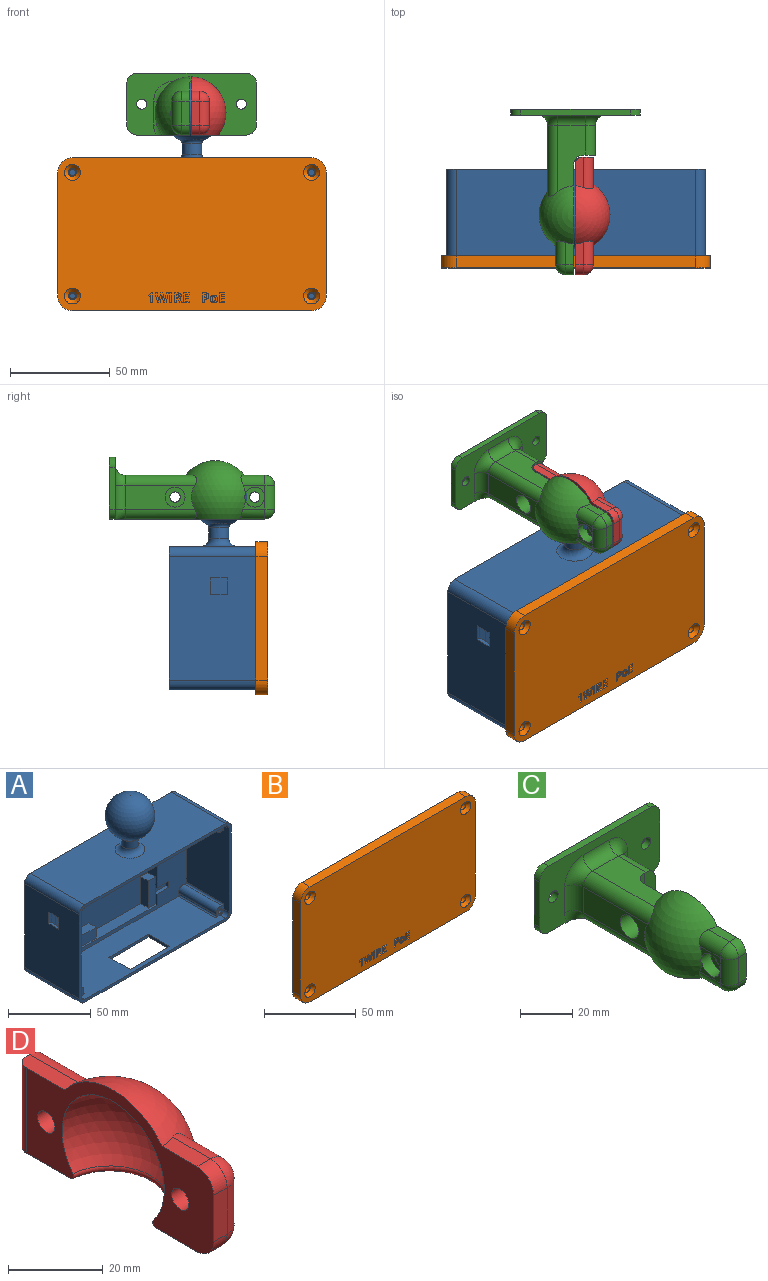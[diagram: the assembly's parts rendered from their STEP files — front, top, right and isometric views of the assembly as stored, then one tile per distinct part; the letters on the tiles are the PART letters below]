
ASSEMBLY  parts=4 mates=1
PART A: 92 faces, bbox 130x46.5x112 mm
  f0: plane 126x68mm, normal (0,-1,0), area 3388mm2, adj f1,f3,f4,f5,f6,f9,f10,f24
  f1: plane 43.9x8mm, normal (-1,0,0), area 302.4mm2, adj f0,f8,f9,f34,f36,f89
  f2: plane 11x9mm, normal (0,-1,0), area 99mm2, adj f6,f9,f81,f82
  f3: plane 120x36.5mm, normal (0,0,1), area 3510mm2, adj f0,f11,f20,f23,f49,f50,f51,f52
  f4: plane 62x36.5mm, normal (-1,0,0), area 2005mm2, adj f0,f11,f20,f21,f59,f66,f70,f74
  f5: plane 62x36.5mm, normal (1,0,0), area 1932.8mm2, adj f0,f11,f22,f23,f45,f46,f47,f48
  f6: plane 120x36.5mm, normal (0,0,-1), area 3994mm2, adj f0,f2,f11,f21,f22,f53,f59,f73
  f7: plane 62x46.5mm, normal (-1,0,0), area 2810.8mm2, adj f11,f15,f18,f19,f45,f46,f47,f48
  f8: plane 86.4x56.4mm, normal (0,-1,0), area 4466.6mm2, adj f1,f9,f24,f25,f26,f27,f28,f29
  f9: plane 85.4x8mm, normal (0,0,-1), area 514.2mm2, adj f0,f1,f2,f8,f24,f37,f38,f44
  f10: plane 8x1.5mm, normal (-1,0,0), area 12mm2, adj f0,f25,f36,f88
  f11: plane 130x72mm, normal (0,-1,0), area 778.3mm2, adj f3,f4,f5,f6,f7,f12,f13,f14
  f12: plane 120x46.5mm, normal (0,0,-1), area 4968mm2, adj f11,f15,f16,f19,f49,f50,f51,f52
  f13: plane 62x46.5mm, normal (1,0,0), area 2883mm2, adj f11,f15,f16,f17
  f14: plane 120x46.5mm, normal (0,0,1), area 5325.5mm2, adj f11,f15,f17,f18,f79
  f15: plane 130x72mm, normal (0,1,0), area 9338.5mm2, adj f7,f12,f13,f14,f16,f17,f18,f19
  f16: cylinder r=5mm len=46.5mm, axis (0,-1,0), area 365.2mm2, adj f11,f12,f13,f15
  f17: cylinder r=5mm len=46.5mm, axis (0,1,0), area 365.2mm2, adj f11,f13,f14,f15
  f18: cylinder r=5mm len=46.5mm, axis (0,-1,0), area 365.2mm2, adj f7,f11,f14,f15
  f19: cylinder r=5mm len=46.5mm, axis (0,1,0), area 365.2mm2, adj f7,f11,f12,f15
  f20: cylinder r=3mm len=4.5mm, axis (0,-1,0), area 21.2mm2, adj f3,f4,f11,f66
  f21: cylinder r=3mm len=4.5mm, axis (0,1,0), area 21.2mm2, adj f4,f6,f11,f59
  f22: cylinder r=3mm len=4.5mm, axis (0,-1,0), area 21.2mm2, adj f5,f6,f11,f53
  f23: cylinder r=3mm len=4.5mm, axis (0,1,0), area 21.2mm2, adj f3,f5,f11,f62
  f24: plane 11.5x8mm, normal (1,0,0), area 92mm2, adj f0,f8,f9,f29
  f25: plane 85.4x8mm, normal (0,0,1), area 546.7mm2, adj f0,f8,f10,f26,f30,f31,f33,f35
  f26: plane 14.9x8mm, normal (1,0,0), area 119.2mm2, adj f0,f8,f25,f27
  f27: plane 8x1mm, normal (0,0,1), area 8mm2, adj f0,f8,f26,f28
  f28: plane 30x8mm, normal (1,0,0), area 240mm2, adj f0,f8,f27,f29
  f29: plane 8x1mm, normal (0,0,-1), area 8mm2, adj f0,f8,f24,f28
  f30: plane 8x6.5mm, normal (-1,0,0), area 52mm2, adj f8,f25,f32,f33
  f31: plane 8x6.5mm, normal (1,0,0), area 52mm2, adj f8,f25,f32,f33
  f32: plane 15x6.5mm, normal (0,0,1), area 97.5mm2, adj f8,f30,f31,f33
  f33: plane 15x8mm, normal (0,-1,0), area 120mm2, adj f25,f30,f31,f32
  f34: plane 6.5x6mm, normal (0,0,1), area 39mm2, adj f1,f8,f35,f36
  f35: plane 20x6.5mm, normal (-1,0,0), area 130mm2, adj f8,f25,f34,f36
  f36: plane 20x6mm, normal (0,-1,0), area 120mm2, adj f1,f10,f25,f34,f35,f86
  f37: plane 6.5x6mm, normal (1,0,0), area 39mm2, adj f8,f9,f43,f44
  f38: plane 6.5x6mm, normal (-1,0,0), area 39mm2, adj f8,f9,f39,f44
  f39: plane 6.5x5mm, normal (0,0,-1), area 32.5mm2, adj f8,f38,f40,f44
  f40: plane 6.5x2mm, normal (1,0,0), area 13mm2, adj f8,f39,f41,f44
  f41: plane 8x6.5mm, normal (0,0,-1), area 52mm2, adj f8,f40,f42,f44
  f42: plane 6.5x2mm, normal (-1,0,0), area 13mm2, adj f8,f41,f43,f44
  f43: plane 13x6.5mm, normal (0,0,-1), area 84.5mm2, adj f8,f37,f42,f44
  f44: plane 26x6mm, normal (0,-1,0), area 140mm2, adj f9,f37,f38,f39,f40,f41,f42,f43
  f45: plane 8.5x2mm, normal (0,0,1), area 17mm2, adj f5,f7,f46,f48
  f46: plane 8.5x2mm, normal (0,1,0), area 17mm2, adj f5,f7,f45,f47
  f47: plane 8.5x2mm, normal (0,0,-1), area 17mm2, adj f5,f7,f46,f48
  f48: plane 8.5x2mm, normal (0,-1,0), area 17mm2, adj f5,f7,f45,f47
  f49: plane 18x2mm, normal (1,0,0), area 36mm2, adj f3,f12,f50,f51
  f50: plane 34x2mm, normal (0,1,0), area 68mm2, adj f3,f12,f49,f52
  f51: plane 34x2mm, normal (0,-1,0), area 68mm2, adj f3,f12,f49,f52
  f52: plane 18x2mm, normal (-1,0,0), area 36mm2, adj f3,f12,f50,f51
  f53: plane 7.03x7.03mm, normal (0,-1,0), area 29.4mm2, adj f5,f6,f22,f54,f55,f75,f76
  f54: cylinder r=3.5mm len=32mm, axis (0,1,0), area 279.1mm2, adj f0,f53,f75,f76
  f55: cylinder r=1.5mm len=32mm, axis (0,1,0), area 301.6mm2, adj f53,f56
  f56: plane 3x3mm, normal (0,-1,0), area 7.1mm2, adj f55
  f57: cylinder r=3.5mm len=32mm, axis (0,1,0), area 279.1mm2, adj f0,f59,f73,f74
  f58: cylinder r=1.5mm len=32mm, axis (0,1,0), area 301.6mm2, adj f59,f60
  f59: plane 7.03x7.03mm, normal (0,-1,0), area 29.4mm2, adj f4,f6,f21,f57,f58,f73,f74
  f60: plane 3x3mm, normal (0,-1,0), area 7.1mm2, adj f58
  f61: cylinder r=3.5mm len=32mm, axis (0,1,0), area 279.1mm2, adj f0,f62,f71,f72
  f62: plane 7.03x7.03mm, normal (0,-1,0), area 29.4mm2, adj f3,f5,f23,f61,f63,f71,f72
  f63: cylinder r=1.5mm len=32mm, axis (0,1,0), area 301.6mm2, adj f62,f64
  f64: plane 3x3mm, normal (0,-1,0), area 7.1mm2, adj f63
  f65: cylinder r=3.5mm len=32mm, axis (0,1,0), area 279.1mm2, adj f0,f66,f69,f70
  f66: plane 7.03x7.03mm, normal (0,-1,0), area 29.4mm2, adj f3,f4,f20,f65,f67,f69,f70
  f67: cylinder r=1.5mm len=32mm, axis (0,1,0), area 301.6mm2, adj f66,f68
  f68: plane 3x3mm, normal (0,-1,0), area 7.1mm2, adj f67
  f69: cylinder r=1mm len=32mm, axis (0,1,0), area 65mm2, adj f0,f3,f65,f66
  f70: cylinder r=1mm len=32mm, axis (0,1,0), area 65mm2, adj f0,f4,f65,f66
  f71: cylinder r=1mm len=32mm, axis (0,1,0), area 65mm2, adj f0,f5,f61,f62
  f72: cylinder r=1mm len=32mm, axis (0,1,0), area 65mm2, adj f0,f3,f61,f62
  f73: cylinder r=1mm len=32mm, axis (0,1,0), area 65mm2, adj f0,f6,f57,f59
  f74: cylinder r=1mm len=32mm, axis (0,1,0), area 65mm2, adj f0,f4,f57,f59
  f75: cylinder r=1mm len=32mm, axis (0,1,0), area 65mm2, adj f0,f5,f53,f54
  f76: cylinder r=1mm len=32mm, axis (0,1,0), area 65mm2, adj f0,f6,f53,f54
  f77: cylinder r=5mm len=10mm, axis (0,0,-1), area 173mm2, adj f79,f91
  f78: sphere r=15mm, area 2702mm2, adj f91
  f79: torus R=9mm, axis (0,0,-1), area 254.8mm2, adj f14,f77
  f80: plane 32x9mm, normal (-1,0,0), area 144mm2, adj f0,f6,f85
  f81: plane 32x9mm, normal (1,0,0), area 144mm2, adj f2,f6,f85
  f82: plane 32x9mm, normal (-1,0,0), area 144mm2, adj f2,f6,f84
  f83: plane 32x9mm, normal (1,0,0), area 144mm2, adj f0,f6,f84
  f84: plane 32x9mm, normal (0,-0.27,-0.96), area 66.5mm2, adj f6,f9,f82,f83
  f85: plane 32x9mm, normal (0,-0.27,-0.96), area 66.5mm2, adj f6,f9,f80,f81
  f86: plane 4.5x1mm, normal (1,0,0), area 4.5mm2, adj f36,f87,f88,f89
  f87: plane 10x4.5mm, normal (0,-1,0), area 45mm2, adj f86,f88,f89,f90
  f88: plane 10x2.5mm, normal (0,0,1), area 25mm2, adj f0,f10,f86,f87,f90
  f89: plane 10x2.5mm, normal (0,0,-1), area 25mm2, adj f0,f1,f86,f87,f90
  f90: plane 4.5x2.5mm, normal (-1,0,0), area 11.3mm2, adj f0,f87,f88,f89
  f91: torus R=7mm, axis (0,0,1), area 77.9mm2, adj f77,f78
PART B: 174 faces, bbox 134.8x6x76.8 mm
  f0: plane 47x3mm, normal (-1,0,0), area 141mm2, adj f1,f166,f170,f171
  f1: plane 125.2x67.2mm, normal (0,1,0), area 3011.4mm2, adj f0,f21,f22,f23,f24,f25,f26,f27
  f2: plane 120x6mm, normal (0,0,-1), area 644mm2, adj f4,f8,f9,f12,f163,f164,f165
  f3: plane 120x3mm, normal (0,0,1), area 284mm2, adj f8,f15,f16,f20,f163,f164,f165
  f4: plane 134.8x76.8mm, normal (0,-1,0), area 10019.4mm2, adj f2,f5,f6,f7,f9,f10,f11,f12
  f5: plane 62x6mm, normal (1,0,0), area 372mm2, adj f4,f8,f9,f10
  f6: plane 120x6mm, normal (0,0,1), area 720mm2, adj f4,f8,f10,f11
  f7: plane 62x6mm, normal (-1,0,0), area 372mm2, adj f4,f8,f11,f12
  f8: plane 134.8x76.8mm, normal (0,1,0), area 732.4mm2, adj f2,f3,f5,f6,f7,f9,f10,f11
  f9: cylinder r=7.4mm len=7.4mm, axis (0,-1,0), area 69.7mm2, adj f2,f4,f5,f8
  f10: cylinder r=7.4mm len=7.4mm, axis (0,1,0), area 69.7mm2, adj f4,f5,f6,f8
  f11: cylinder r=7.4mm len=7.4mm, axis (0,-1,0), area 69.7mm2, adj f4,f6,f7,f8
  f12: cylinder r=7.4mm len=7.4mm, axis (0,1,0), area 69.7mm2, adj f2,f4,f7,f8
  f13: cylinder r=5.4mm len=5.4mm, axis (0,1,0), area 25.4mm2, adj f8,f14,f19,f20
  f14: plane 62x3mm, normal (1,0,0), area 186mm2, adj f8,f13,f15,f20
  f15: cylinder r=5.4mm len=5.4mm, axis (0,1,0), area 25.4mm2, adj f3,f8,f14,f20
  f16: cylinder r=5.4mm len=5.4mm, axis (0,1,0), area 25.4mm2, adj f3,f8,f17,f20
  f17: plane 62x3mm, normal (-1,0,0), area 186mm2, adj f8,f16,f18,f20
  f18: cylinder r=5.4mm len=5.4mm, axis (0,1,0), area 25.4mm2, adj f8,f17,f19,f20
  f19: plane 120x3mm, normal (0,0,-1), area 360mm2, adj f8,f13,f18,f20
  f20: plane 130.8x72.8mm, normal (0,1,0), area 1089.6mm2, adj f3,f13,f14,f15,f16,f17,f18,f19
  f21: plane 62x3mm, normal (-1,0,0), area 186mm2, adj f1,f20,f22,f26
  f22: cylinder r=2.6mm len=3mm, axis (0,1,0), area 12.3mm2, adj f1,f20,f21,f23
  f23: plane 120x3mm, normal (0,0,-1), area 360mm2, adj f1,f20,f22,f24
  f24: cylinder r=2.6mm len=3mm, axis (0,1,0), area 12.3mm2, adj f1,f20,f23,f25
  f25: plane 62x3mm, normal (1,0,0), area 186mm2, adj f1,f20,f24,f27
  f26: cylinder r=2.6mm len=3mm, axis (0,1,0), area 12.3mm2, adj f1,f20,f21,f28
  f27: cylinder r=2.6mm len=3mm, axis (0,1,0), area 12.3mm2, adj f1,f20,f25,f28
  f28: plane 120x3mm, normal (0,0,1), area 360mm2, adj f1,f20,f26,f27
  f29: cylinder r=2mm len=4mm, axis (0,1,0), area 50.3mm2, adj f1,f35
  f30: cylinder r=2mm len=4mm, axis (0,1,0), area 50.3mm2, adj f1,f36
  f31: cylinder r=2mm len=4mm, axis (0,1,0), area 50.3mm2, adj f1,f33
  f32: cylinder r=2mm len=4mm, axis (0,1,0), area 50.3mm2, adj f1,f34
  f33: cone r=2mm half-angle=45deg, axis (0,-1,0), area 53.3mm2, adj f4,f31
  f34: cone r=2mm half-angle=45deg, axis (0,-1,0), area 53.3mm2, adj f4,f32
  f35: cone r=2mm half-angle=45deg, axis (0,-1,0), area 53.3mm2, adj f4,f29
  f36: cone r=2mm half-angle=45deg, axis (0,-1,0), area 53.3mm2, adj f4,f30
  f37: plane 1.2x1mm, normal (0,0,1), area 1.2mm2, adj f4,f38,f60,f61
  f38: plane 4.96x1.26mm, normal (-0.97,0,0.25), area 5.1mm2, adj f4,f37,f39,f61
  f39: plane 1.04x1mm, normal (0,0,-1), area 1mm2, adj f4,f38,f40,f61
  f40: plane 2.71x1mm, normal (0.97,0,-0.23), area 2.8mm2, adj f4,f39,f41,f61
  f41: extruded ~1x0.64mm, area 0.7mm2, adj f4,f40,f42,f61
  f42: extruded ~1x0.66mm, area 0.7mm2, adj f4,f41,f43,f61
  f43: extruded ~1x0.66mm, area 0.7mm2, adj f4,f42,f44,f61
  f44: extruded ~1x0.57mm, area 0.6mm2, adj f4,f43,f45,f61
  f45: plane 2.78x1mm, normal (-0.97,0,-0.25), area 2.9mm2, adj f4,f44,f46,f61
  f46: plane 1x0.99mm, normal (0,0,-1), area 1mm2, adj f4,f45,f47,f61
  f47: plane 2.78x1mm, normal (0.97,0,-0.25), area 2.9mm2, adj f4,f46,f48,f61
  f48: extruded ~1x0.63mm, area 0.6mm2, adj f4,f47,f49,f61
  f49: extruded ~1x0.6mm, area 0.6mm2, adj f4,f48,f50,f61
  f50: extruded ~1.3x1mm, area 1.3mm2, adj f4,f49,f51,f61
  f51: plane 2.71x1mm, normal (-0.97,0,-0.23), area 2.8mm2, adj f4,f50,f52,f61
  f52: plane 1.03x1mm, normal (0,0,-1), area 1mm2, adj f4,f51,f53,f61
  f53: plane 4.96x1.27mm, normal (0.97,0,0.25), area 5.1mm2, adj f4,f52,f54,f61
  f54: plane 1.19x1mm, normal (0,0,1), area 1.2mm2, adj f4,f53,f55,f61
  f55: plane 2.6x1mm, normal (-0.97,0,0.25), area 2.7mm2, adj f4,f54,f56,f61
  f56: extruded ~1x0.58mm, area 0.6mm2, adj f4,f55,f57,f61
  f57: extruded ~1x0.59mm, area 0.6mm2, adj f4,f56,f58,f61
  f58: extruded ~1x0.59mm, area 0.6mm2, adj f4,f57,f59,f61
  f59: extruded ~1x0.57mm, area 0.6mm2, adj f4,f58,f60,f61
  f60: plane 2.6x1mm, normal (0.97,0,0.25), area 2.7mm2, adj f4,f37,f59,f61
  f61: plane 6.71x4.96mm, normal (0,-1,0), area 17mm2, adj f37,f38,f39,f40,f41,f42,f43,f44
  f62: plane 4.96x1mm, normal (1,0,0), area 5mm2, adj f4,f63,f65,f66
  f63: plane 1.05x1mm, normal (0,0,1), area 1.1mm2, adj f4,f62,f64,f66
  f64: plane 4.96x1mm, normal (-1,0,0), area 5mm2, adj f4,f63,f65,f66
  f65: plane 1.05x1mm, normal (0,0,-1), area 1.1mm2, adj f4,f62,f64,f66
  f66: plane 4.96x1.05mm, normal (0,-1,0), area 5.2mm2, adj f62,f63,f64,f65
  f67: plane 2.86x1mm, normal (0,0,1), area 2.9mm2, adj f4,f68,f78,f79
  f68: plane 1x0.87mm, normal (-1,0,0), area 0.9mm2, adj f4,f67,f69,f79
  f69: plane 1.8x1mm, normal (0,0,-1), area 1.8mm2, adj f4,f68,f70,f79
  f70: plane 1.28x1mm, normal (-1,0,0), area 1.3mm2, adj f4,f69,f71,f79
  f71: plane 1.68x1mm, normal (0,0,1), area 1.7mm2, adj f4,f70,f72,f79
  f72: plane 1x0.86mm, normal (-1,0,0), area 0.9mm2, adj f4,f71,f73,f79
  f73: plane 1.68x1mm, normal (0,0,-1), area 1.7mm2, adj f4,f72,f74,f79
  f74: plane 1.09x1mm, normal (-1,0,0), area 1.1mm2, adj f4,f73,f75,f79
  f75: plane 1.8x1mm, normal (0,0,1), area 1.8mm2, adj f4,f74,f76,f79
  f76: plane 1x0.86mm, normal (-1,0,0), area 0.9mm2, adj f4,f75,f77,f79
  f77: plane 2.86x1mm, normal (0,0,-1), area 2.9mm2, adj f4,f76,f78,f79
  f78: plane 4.96x1mm, normal (1,0,0), area 5mm2, adj f4,f67,f77,f79
  f79: plane 4.96x2.86mm, normal (0,-1,0), area 9.8mm2, adj f67,f68,f69,f70,f71,f72,f73,f74
  f80: plane 2.86x1mm, normal (0,0,1), area 2.9mm2, adj f4,f81,f91,f92
  f81: plane 1x0.87mm, normal (-1,0,0), area 0.9mm2, adj f4,f80,f82,f92
  f82: plane 1.8x1mm, normal (0,0,-1), area 1.8mm2, adj f4,f81,f83,f92
  f83: plane 1.28x1mm, normal (-1,0,0), area 1.3mm2, adj f4,f82,f84,f92
  f84: plane 1.68x1mm, normal (0,0,1), area 1.7mm2, adj f4,f83,f85,f92
  f85: plane 1x0.86mm, normal (-1,0,0), area 0.9mm2, adj f4,f84,f86,f92
  f86: plane 1.68x1mm, normal (0,0,-1), area 1.7mm2, adj f4,f85,f87,f92
  f87: plane 1.09x1mm, normal (-1,0,0), area 1.1mm2, adj f4,f86,f88,f92
  f88: plane 1.8x1mm, normal (0,0,1), area 1.8mm2, adj f4,f87,f89,f92
  f89: plane 1x0.86mm, normal (-1,0,0), area 0.9mm2, adj f4,f88,f90,f92
  f90: plane 2.86x1mm, normal (0,0,-1), area 2.9mm2, adj f4,f89,f91,f92
  f91: plane 4.96x1mm, normal (1,0,0), area 5mm2, adj f4,f80,f90,f92
  f92: plane 4.96x2.86mm, normal (0,-1,0), area 9.8mm2, adj f80,f81,f82,f83,f84,f85,f86,f87
  f93: plane 1.9x1mm, normal (-1,0,0), area 1.9mm2, adj f4,f94,f111,f112
  f94: plane 1x0.56mm, normal (0,0,1), area 0.6mm2, adj f4,f93,f95,f112
  f95: plane 1.9x1.18mm, normal (0.85,0,0.53), area 2.2mm2, adj f4,f94,f96,f112
  f96: plane 1.17x1mm, normal (0,0,1), area 1.2mm2, adj f4,f95,f97,f112
  f97: extruded ~2.16x1.46mm, area 2.6mm2, adj f4,f96,f98,f112
  f98: extruded ~1x0.68mm, area 0.9mm2, adj f4,f97,f99,f112
  f99: extruded ~1x0.78mm, area 0.8mm2, adj f4,f98,f100,f112
  f100: extruded ~1.12x1mm, area 1.3mm2, adj f4,f99,f101,f112
  f101: extruded ~1.5x1mm, area 1.6mm2, adj f4,f100,f102,f112
  f102: plane 1.44x1mm, normal (0,0,-1), area 1.4mm2, adj f4,f101,f103,f112
  f103: plane 4.96x1mm, normal (1,0,0), area 5mm2, adj f4,f102,f111,f112
  f104: plane 1x0.34mm, normal (0,0,-1), area 0.3mm2, adj f105,f110,f112,f113
  f105: plane 1.34x1mm, normal (-1,0,0), area 1.3mm2, adj f104,f106,f112,f113
  f106: plane 1x0.32mm, normal (0,0,1), area 0.3mm2, adj f105,f107,f112,f113
  f107: extruded ~1x0.75mm, area 0.8mm2, adj f106,f108,f112,f113
  f108: extruded ~1x0.5mm, area 0.6mm2, adj f107,f109,f112,f113
  f109: extruded ~1x0.52mm, area 0.6mm2, adj f108,f110,f112,f113
  f110: extruded ~1x0.74mm, area 0.8mm2, adj f104,f109,f112,f113
  f111: plane 1.05x1mm, normal (0,0,1), area 1.1mm2, adj f4,f93,f103,f112
  f112: plane 4.96x3.96mm, normal (0,-1,0), area 12mm2, adj f93,f94,f95,f96,f97,f98,f99,f100
  f113: plane 1.34x1.31mm, normal (0,-1,0), area 1.6mm2, adj f104,f105,f106,f107,f108,f109,f110
  f114: extruded ~1.22x1mm, area 1.4mm2, adj f4,f115,f129,f130
  f115: extruded ~1.16x1mm, area 1.3mm2, adj f4,f114,f116,f130
  f116: extruded ~1.37x1mm, area 1.5mm2, adj f4,f115,f117,f130
  f117: plane 1.58x1mm, normal (0,0,-1), area 1.6mm2, adj f4,f116,f118,f130
  f118: plane 4.96x1mm, normal (1,0,0), area 5mm2, adj f4,f117,f119,f130
  f119: plane 1.05x1mm, normal (0,0,1), area 1.1mm2, adj f4,f118,f120,f130
  f120: plane 1.76x1mm, normal (-1,0,0), area 1.8mm2, adj f4,f119,f121,f130
  f121: plane 1x0.45mm, normal (0,0,1), area 0.5mm2, adj f4,f120,f129,f130
  f122: plane 1x0.35mm, normal (0,0,-1), area 0.3mm2, adj f123,f128,f130,f131
  f123: plane 1.47x1mm, normal (-1,0,0), area 1.5mm2, adj f122,f124,f130,f131
  f124: plane 1x0.48mm, normal (0,0,1), area 0.5mm2, adj f123,f125,f130,f131
  f125: extruded ~1x0.63mm, area 0.7mm2, adj f124,f126,f130,f131
  f126: extruded ~1x0.55mm, area 0.6mm2, adj f125,f127,f130,f131
  f127: extruded ~1x0.56mm, area 0.6mm2, adj f126,f128,f130,f131
  f128: extruded ~1x0.73mm, area 0.8mm2, adj f122,f127,f130,f131
  f129: extruded ~1.42x1mm, area 1.5mm2, adj f4,f114,f121,f130
  f130: plane 4.96x3.42mm, normal (0,-1,0), area 10mm2, adj f114,f115,f116,f117,f118,f119,f120,f121
  f131: plane 1.47x1.31mm, normal (0,-1,0), area 1.7mm2, adj f122,f123,f124,f125,f126,f127,f128
  f132: extruded ~1.45x1mm, area 1.6mm2, adj f4,f133,f149,f150
  f133: extruded ~1.04x1mm, area 1.1mm2, adj f4,f132,f134,f150
  f134: extruded ~1x0.68mm, area 0.9mm2, adj f4,f133,f135,f150
  f135: extruded ~1x0.96mm, area 1mm2, adj f4,f134,f136,f150
  f136: extruded ~1.36x1mm, area 1.5mm2, adj f4,f135,f137,f150
  f137: extruded ~1.44x1mm, area 1.6mm2, adj f4,f136,f138,f150
  f138: extruded ~1.04x1mm, area 1.1mm2, adj f4,f137,f139,f150
  f139: extruded ~1x0.69mm, area 1mm2, adj f4,f138,f140,f150
  f140: extruded ~1x0.96mm, area 1mm2, adj f4,f139,f149,f150
  f141: extruded ~1x0.85mm, area 0.9mm2, adj f142,f148,f150,f151
  f142: extruded ~1x0.85mm, area 0.9mm2, adj f141,f143,f150,f151
  f143: extruded ~1x0.6mm, area 0.7mm2, adj f142,f144,f150,f151
  f144: extruded ~1x0.6mm, area 0.7mm2, adj f143,f145,f150,f151
  f145: extruded ~1x0.84mm, area 0.9mm2, adj f144,f146,f150,f151
  f146: extruded ~1x0.85mm, area 0.9mm2, adj f145,f147,f150,f151
  f147: extruded ~1x0.6mm, area 0.7mm2, adj f146,f148,f150,f151
  f148: extruded ~1x0.6mm, area 0.7mm2, adj f141,f147,f150,f151
  f149: extruded ~1.36x1mm, area 1.5mm2, adj f4,f132,f140,f150
  f150: plane 3.93x3.68mm, normal (0,-1,0), area 8.8mm2, adj f132,f133,f134,f135,f136,f137,f138,f139
  f151: plane 2.27x1.56mm, normal (0,-1,0), area 3mm2, adj f141,f142,f143,f144,f145,f146,f147,f148
  f152: plane 1.05x1mm, normal (0,0,1), area 1mm2, adj f4,f153,f161,f162
  f153: plane 4.96x1mm, normal (-1,0,0), area 5mm2, adj f4,f152,f154,f162
  f154: plane 1x0.86mm, normal (0,0,-1), area 0.9mm2, adj f4,f153,f155,f162
  f155: plane 1.6x1.27mm, normal (0.62,0,-0.78), area 2mm2, adj f4,f154,f156,f162
  f156: plane 1x0.63mm, normal (0.78,0,0.63), area 0.8mm2, adj f4,f155,f157,f162
  f157: plane 1x0.57mm, normal (-0.63,0,0.78), area 0.7mm2, adj f4,f156,f158,f162
  f158: extruded ~1x0.36mm, area 0.5mm2, adj f4,f157,f159,f162
  f159: plane 1x0.52mm, normal (1,0,-0.03), area 0.5mm2, adj f4,f158,f160,f162
  f160: plane 1x0.47mm, normal (1,0,-0.02), area 0.5mm2, adj f4,f159,f161,f162
  f161: plane 2.87x1mm, normal (1,0,0), area 2.9mm2, adj f4,f152,f160,f162
  f162: plane 4.96x2.46mm, normal (0,-1,0), area 6.4mm2, adj f152,f153,f154,f155,f156,f157,f158,f159
  f163: plane 2x2mm, normal (1,0,0), area 4mm2, adj f2,f3,f8,f165
  f164: plane 2x2mm, normal (-1,0,0), area 4mm2, adj f2,f3,f8,f165
  f165: plane 38x2mm, normal (0,1,0), area 76mm2, adj f2,f3,f163,f164
  f166: plane 90x3mm, normal (0,0,-1), area 270mm2, adj f0,f1,f169,f170
  f167: plane 6x3mm, normal (-1,0,0), area 18mm2, adj f1,f168,f170,f173
  f168: plane 90x3mm, normal (0,0,1), area 270mm2, adj f1,f167,f169,f170
  f169: plane 59x3mm, normal (1,0,0), area 177mm2, adj f1,f166,f168,f170
  f170: plane 96x59mm, normal (0,1,0), area 5346mm2, adj f0,f166,f167,f168,f169,f171,f172,f173
  f171: plane 6x3mm, normal (0,0,-1), area 18mm2, adj f0,f1,f170,f172
  f172: plane 6x3mm, normal (-1,0,0), area 18mm2, adj f1,f170,f171,f173
  f173: plane 6x3mm, normal (0,0,1), area 18mm2, adj f1,f167,f170,f172
PART C: 49 faces, bbox 65.2x83.2x37 mm
  f0: plane 11.11x6.21mm, normal (-1,0,0), area 21.5mm2, adj f1,f24,f29,f34
  f1: sphere r=18.3mm, area 1045.4mm2, adj f0,f4,f8,f11,f12,f14,f15,f24
  f2: cylinder r=2.6mm len=5.2mm, axis (1,0,0), area 65.3mm2, adj f4,f25
  f3: cylinder r=2.6mm len=5.2mm, axis (1,0,0), area 65.3mm2, adj f4,f22
  f4: plane 55x29.27mm, normal (1,0,0), area 632.9mm2, adj f1,f2,f3,f7,f8,f9,f10,f11
  f5: plane 65x31mm, normal (0,-1,0), area 1083.5mm2, adj f8,f17,f18,f19,f20,f21,f37,f38
  f6: plane 65x31mm, normal (0,1,0), area 1954.3mm2, adj f8,f17,f18,f19,f20,f21,f37,f38
  f7: plane 12x4mm, normal (0,-1,0), area 48mm2, adj f4,f32,f34,f36
  f8: plane 78x55mm, normal (0,0,-1), area 727.3mm2, adj f1,f4,f5,f6,f10,f16,f26,f29
  f9: sphere r=15.3mm, area 1117.9mm2, adj f4,f10
  f10: torus R=12.87mm, axis (0,0,-1), area 80.7mm2, adj f4,f8,f9
  f11: plane 33.47x14mm, normal (0,0,1), area 347.2mm2, adj f1,f4,f16,f27,f30,f44,f48
  f12: plane 34.86x12mm, normal (-1,0,0), area 326.4mm2, adj f1,f23,f30,f31,f42
  f13: plane 15x12mm, normal (1,0,0), area 180mm2, adj f16,f26,f27,f46
  f14: plane 11.26x4mm, normal (0,0,1), area 42.9mm2, adj f1,f4,f28,f36
  f15: plane 11.11x6.21mm, normal (-1,0,0), area 21.5mm2, adj f1,f24,f28,f34
  f16: plane 22x6mm, normal (0,-1,0), area 121.3mm2, adj f8,f11,f13,f26,f27,f48
  f17: plane 21x3mm, normal (1,0,0), area 63mm2, adj f5,f6,f39,f40
  f18: plane 21x3mm, normal (-1,0,0), area 63mm2, adj f5,f6,f37,f38
  f19: plane 55x3mm, normal (0,0,1), area 165mm2, adj f5,f6,f38,f39
  f20: cylinder r=2.5mm len=5mm, axis (0,-1,0), area 47.1mm2, adj f5,f6
  f21: cylinder r=2.5mm len=5mm, axis (0,-1,0), area 47.1mm2, adj f5,f6
  f22: plane 10x10mm, normal (-1,0,0), area 57.3mm2, adj f3,f23
  f23: cylinder r=5mm len=10mm, axis (-1,0,0), area 282.7mm2, adj f12,f22
  f24: cylinder r=5mm len=10mm, axis (-1,0,0), area 158.1mm2, adj f0,f1,f15,f25
  f25: plane 10x10mm, normal (-1,0,0), area 57.3mm2, adj f2,f24
  f26: cylinder r=5mm len=15mm, axis (0,1,0), area 117.8mm2, adj f8,f13,f16,f47
  f27: cylinder r=5mm len=15mm, axis (0,1,0), area 117.8mm2, adj f11,f13,f16,f45
  f28: cylinder r=5mm len=11.93mm, axis (0,-1,0), area 91.3mm2, adj f1,f14,f15,f35
  f29: cylinder r=5mm len=11.93mm, axis (0,-1,0), area 91.3mm2, adj f0,f1,f8,f33
  f30: cylinder r=5mm len=35.8mm, axis (0,-1,0), area 276.1mm2, adj f1,f11,f12,f43
  f31: cylinder r=5mm len=35.8mm, axis (0,-1,0), area 276.1mm2, adj f1,f8,f12,f41
  f32: cylinder r=5mm len=5mm, axis (1,0,0), area 31.4mm2, adj f4,f7,f8,f33
  f33: sphere r=5mm, area 39.3mm2, adj f29,f32,f34
  f34: cylinder r=5mm len=12mm, axis (0,0,-1), area 94.2mm2, adj f0,f7,f15,f33,f35
  f35: sphere r=5mm, area 39.3mm2, adj f28,f34,f36
  f36: cylinder r=5mm len=5mm, axis (-1,0,0), area 31.4mm2, adj f4,f7,f14,f35
  f37: cylinder r=5mm len=5mm, axis (0,1,0), area 23.6mm2, adj f5,f6,f8,f18
  f38: cylinder r=5mm len=5mm, axis (0,-1,0), area 23.6mm2, adj f5,f6,f18,f19
  f39: cylinder r=5mm len=5mm, axis (0,1,0), area 23.6mm2, adj f5,f6,f17,f19
  f40: cylinder r=5mm len=5mm, axis (0,-1,0), area 23.6mm2, adj f5,f6,f8,f17
  f41: torus R=10mm, axis (0,1,0), area 47mm2, adj f5,f8,f31,f42
  f42: cylinder r=5mm len=12mm, axis (0,0,1), area 94.2mm2, adj f5,f12,f41,f43
  f43: torus R=10mm, axis (0,1,0), area 84.1mm2, adj f5,f30,f42,f44
  f44: cylinder r=5mm len=14mm, axis (1,0,0), area 110mm2, adj f5,f11,f43,f45
  f45: torus R=10mm, axis (0,1,0), area 84.1mm2, adj f5,f27,f44,f46
  f46: cylinder r=5mm len=12mm, axis (0,0,-1), area 94.2mm2, adj f5,f13,f45,f47
  f47: torus R=10mm, axis (0,1,0), area 47mm2, adj f5,f8,f26,f46
  f48: cylinder r=5mm len=22mm, axis (0,0,-1), area 172.8mm2, adj f4,f8,f11,f16
PART D: 37 faces, bbox 18.3x59x29.3 mm
  f0: plane 12x10.9mm, normal (1,0,0), area 59.8mm2, adj f9,f20,f21,f22,f23,f24,f25,f27
  f1: cylinder r=2.6mm len=5.2mm, axis (1,0,0), area 65.3mm2, adj f3,f26
  f2: cylinder r=2.6mm len=5.2mm, axis (1,0,0), area 65.3mm2, adj f3,f13
  f3: plane 56x29.27mm, normal (-1,0,0), area 654.9mm2, adj f1,f2,f4,f5,f6,f7,f8,f9
  f4: torus R=12.87mm, axis (0,0,-1), area 80.7mm2, adj f3,f5,f6
  f5: sphere r=15.3mm, area 1117.9mm2, adj f3,f4
  f6: plane 54x13.63mm, normal (0,0,-1), area 172.2mm2, adj f3,f4,f9,f12,f28,f29,f35,f36
  f7: plane 11.26x4mm, normal (0,0,1), area 42.9mm2, adj f3,f9,f27,f31
  f8: plane 15.26x4mm, normal (0,0,1), area 57mm2, adj f3,f9,f12,f30,f36
  f9: sphere r=18.3mm, area 1177mm2, adj f0,f3,f6,f7,f8,f11,f27,f28
  f10: plane 12x4mm, normal (0,-1,0), area 48mm2, adj f3,f31,f33,f35
  f11: plane 14.9x12mm, normal (1,0,0), area 107.8mm2, adj f9,f12,f14,f15,f16,f17,f18,f19
  f12: plane 22x6mm, normal (0,1,0), area 121.3mm2, adj f6,f8,f11,f29,f30,f36
  f13: plane 9.7x8.4mm, normal (1,0,0), area 39.9mm2, adj f2,f14,f15,f16,f17,f18,f19
  f14: plane 5x4.2mm, normal (0,-0.5,0.87), area 24.2mm2, adj f11,f13,f15,f19
  f15: plane 5x4.85mm, normal (0,-1,0), area 24.2mm2, adj f11,f13,f14,f16
  f16: plane 5x4.2mm, normal (0,-0.5,-0.87), area 24.2mm2, adj f11,f13,f15,f17
  f17: plane 5x4.2mm, normal (0,0.5,-0.87), area 24.2mm2, adj f11,f13,f16,f18
  f18: plane 5x4.85mm, normal (0,1,0), area 24.2mm2, adj f11,f13,f17,f19
  f19: plane 5x4.2mm, normal (0,0.5,0.87), area 24.2mm2, adj f11,f13,f14,f18
  f20: plane 5x4.85mm, normal (0,1,0), area 24.2mm2, adj f0,f21,f25,f26
  f21: plane 5x4.2mm, normal (0,0.5,0.87), area 24.2mm2, adj f0,f20,f22,f26
  f22: plane 5x4.2mm, normal (0,-0.5,0.87), area 24.2mm2, adj f0,f21,f23,f26
  f23: plane 5x4.85mm, normal (0,-1,0), area 24.2mm2, adj f0,f22,f24,f26
  f24: plane 5x4.2mm, normal (0,-0.5,-0.87), area 24.2mm2, adj f0,f23,f25,f26
  f25: plane 5x4.2mm, normal (0,0.5,-0.87), area 24.2mm2, adj f0,f20,f24,f26
  f26: plane 9.7x8.4mm, normal (1,0,0), area 39.9mm2, adj f1,f20,f21,f22,f23,f24,f25
  f27: cylinder r=5mm len=11.93mm, axis (0,-1,0), area 91.3mm2, adj f0,f7,f9,f32
  f28: cylinder r=5mm len=11.93mm, axis (0,-1,0), area 91.3mm2, adj f0,f6,f9,f34
  f29: cylinder r=5mm len=15.93mm, axis (0,1,0), area 122.7mm2, adj f6,f9,f11,f12
  f30: cylinder r=5mm len=15.93mm, axis (0,1,0), area 122.7mm2, adj f8,f9,f11,f12
  f31: cylinder r=5mm len=5mm, axis (-1,0,0), area 31.4mm2, adj f3,f7,f10,f32
  f32: sphere r=5mm, area 39.3mm2, adj f27,f31,f33
  f33: cylinder r=5mm len=12mm, axis (0,0,1), area 94.2mm2, adj f0,f10,f32,f34
  f34: sphere r=5mm, area 39.3mm2, adj f28,f33,f35
  f35: cylinder r=5mm len=5mm, axis (1,0,0), area 31.4mm2, adj f3,f6,f10,f34
  f36: cylinder r=3mm len=22mm, axis (0,0,-1), area 103.7mm2, adj f3,f6,f8,f12
PLACE A at identity fixed
PLACE B t=(0,-18.5,0)mm
PLACE C t=(-0.24,2,60.76)mm
PLACE D t=(-1.24,2,60.76)mm
MATE revolute A.f18 <-> B.f11  axis (0,1,0) through (-60,-17,31)mm
